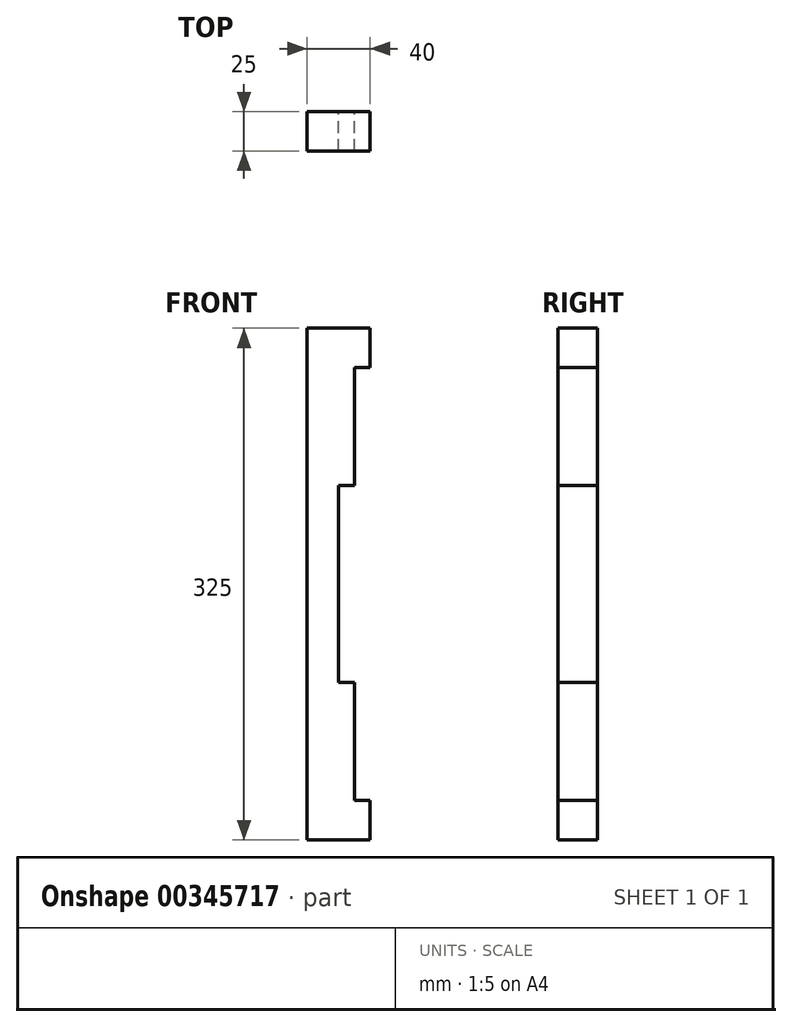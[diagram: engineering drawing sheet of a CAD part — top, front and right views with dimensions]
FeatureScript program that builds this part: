
annotation { "Feature Type Name" : "Feature", "Feature Type Description" : "" }
export const myFeature = defineFeature(function(context is Context, id is Id, definition is map)
    precondition{}
    {
        {
            var Q0;
            Q0=qCreatedBy(makeId("Front.planeOp"),FACE);
            var sketch = newSketch(context, id + "F0", { "sketchPlane" : qUnion([Q0])});
            skLineSegment(sketch, "E0.bottom", {"start": v(-10, 162.5) * mm, "end": v(10, 162.5) * mm});
            skLineSegment(sketch, "E0.top", {"start": v(-10, -162.5) * mm, "end": v(10, -162.5) * mm});
            skLineSegment(sketch, "E0.left", {"start": v(-10, 162.5) * mm, "end": v(-10, -162.5) * mm});
            skLineSegment(sketch, "E0.right", {"start": v(10, 162.5) * mm, "end": v(10, -162.5) * mm});
            skPoint(sketch, "E0.middle", {"position": v(0, 0) * mm});
            skLineSegment(sketch, "E1.bottom", {"start": v(10, 162.5) * mm, "end": v(30, 162.5) * mm});
            skLineSegment(sketch, "E1.top", {"start": v(10, 137.5) * mm, "end": v(30, 137.5) * mm});
            skLineSegment(sketch, "E1.left", {"start": v(10, 162.5) * mm, "end": v(10, 137.5) * mm});
            skLineSegment(sketch, "E1.right", {"start": v(30, 162.5) * mm, "end": v(30, 137.5) * mm});
            skLineSegment(sketch, "E2.bottom", {"start": v(20, 137.5) * mm, "end": v(10, 137.5) * mm});
            skLineSegment(sketch, "E2.top", {"start": v(20, 62.5) * mm, "end": v(10, 62.5) * mm});
            skLineSegment(sketch, "E2.left", {"start": v(20, 137.5) * mm, "end": v(20, 62.5) * mm});
            skLineSegment(sketch, "E2.right", {"start": v(10, 137.5) * mm, "end": v(10, 62.5) * mm});
            skLineSegment(sketch, "E3.MirrorCS", {"start": v(20, -62.5) * mm, "end": v(10, -62.5) * mm});
            skLineSegment(sketch, "E4.MirrorCS", {"start": v(20, -137.5) * mm, "end": v(10, -137.5) * mm});
            skLineSegment(sketch, "E5.MirrorCS", {"start": v(10, -137.5) * mm, "end": v(30, -137.5) * mm});
            skLineSegment(sketch, "E6.MirrorCS", {"start": v(10, -162.5) * mm, "end": v(10, 162.5) * mm});
            skLineSegment(sketch, "E7.MirrorCS", {"start": v(10, -137.5) * mm, "end": v(10, -62.5) * mm});
            skLineSegment(sketch, "E8.MirrorCS", {"start": v(20, -137.5) * mm, "end": v(20, -62.5) * mm});
            skLineSegment(sketch, "E9.MirrorCS", {"start": v(10, -162.5) * mm, "end": v(30, -162.5) * mm});
            skLineSegment(sketch, "E10.MirrorCS", {"start": v(30, -162.5) * mm, "end": v(30, -137.5) * mm});
            skLineSegment(sketch, "E11.MirrorCS", {"start": v(10, -162.5) * mm, "end": v(10, -137.5) * mm});
            skSolve(sketch);
        }
        {
            var Q0;
            Q0 = qSketchRegion(id + "F0", true);
            extrude(context, id + "F1", {"entities" : qUnion([Q0]), "depth" : 25 * mm});
        }
    });
